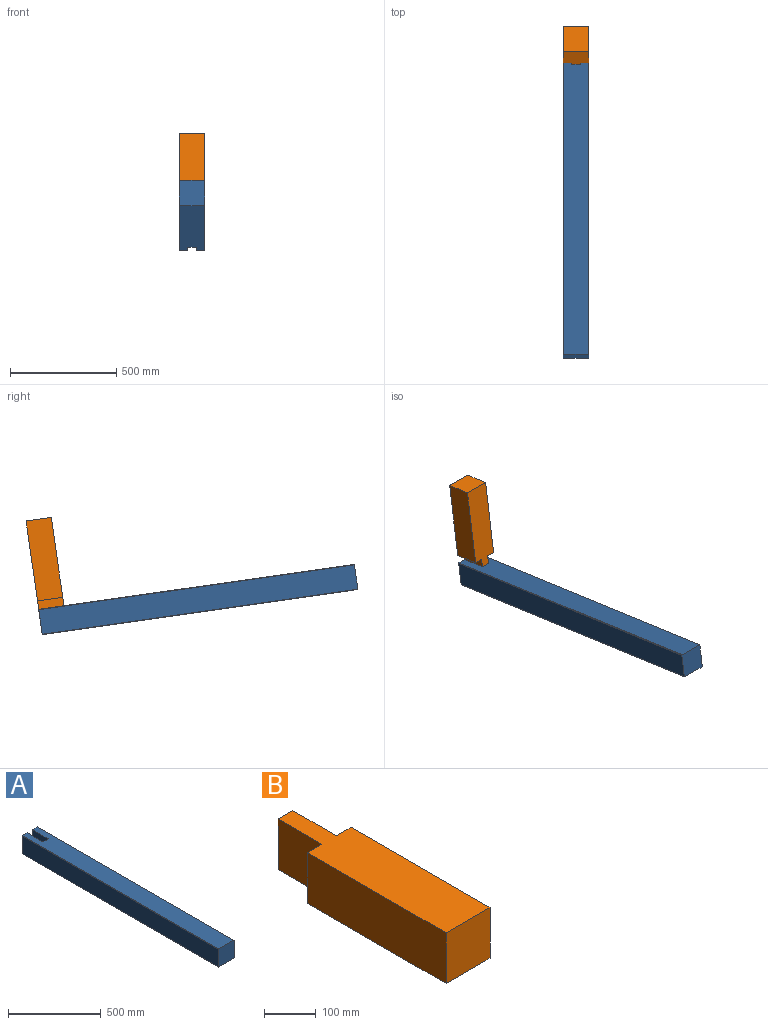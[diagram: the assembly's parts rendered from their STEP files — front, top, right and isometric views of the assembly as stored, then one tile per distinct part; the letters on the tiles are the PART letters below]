
ASSEMBLY  parts=2 mates=2
PART A: 14 faces, bbox 120x1500x120 mm
  f0: plane 120x40mm, normal (0,1,0), area 4796mm2, adj f1,f2,f4,f7,f10,f13
  f1: plane 1500x116mm, normal (0,0,-1), area 169200mm2, adj f0,f5,f6,f7,f8,f11,f12,f13
  f2: plane 1500x116mm, normal (0,0,1), area 169200mm2, adj f0,f5,f6,f9,f10,f11,f12,f13
  f3: plane 1500x116mm, normal (-1,0,0), area 174000mm2, adj f5,f6,f8,f9
  f4: plane 1500x116mm, normal (1,0,0), area 174000mm2, adj f0,f5,f7,f10
  f5: plane 120x120mm, normal (0,-1,0), area 14392mm2, adj f1,f2,f3,f4,f7,f8,f9,f10
  f6: plane 120x40mm, normal (0,1,0), area 4796mm2, adj f1,f2,f3,f8,f9,f11
  f7: plane 1500x2mm, normal (0.71,0,-0.71), area 4242.6mm2, adj f0,f1,f4,f5
  f8: plane 1500x2mm, normal (-0.71,0,-0.71), area 4242.6mm2, adj f1,f3,f5,f6
  f9: plane 1500x2mm, normal (-0.71,0,0.71), area 4242.6mm2, adj f2,f3,f5,f6
  f10: plane 1500x2mm, normal (0.71,0,0.71), area 4242.6mm2, adj f0,f2,f4,f5
  f11: plane 120x120mm, normal (1,0,0), area 14400mm2, adj f1,f2,f6,f12
  f12: plane 120x40mm, normal (0,1,0), area 4800mm2, adj f1,f2,f11,f13
  f13: plane 120x120mm, normal (-1,0,0), area 14400mm2, adj f0,f1,f2,f12
PART B: 10 faces, bbox 120x500x120 mm
  f0: plane 380x120mm, normal (-1,0,0), area 45600mm2, adj f1,f4,f5,f9
  f1: plane 500x120mm, normal (0,0,-1), area 50400mm2, adj f0,f2,f3,f5,f6,f7,f8,f9
  f2: plane 380x120mm, normal (1,0,0), area 45600mm2, adj f1,f4,f5,f7
  f3: plane 120x40mm, normal (0,1,0), area 4800mm2, adj f1,f4,f6,f8
  f4: plane 500x120mm, normal (0,0,1), area 50400mm2, adj f0,f2,f3,f5,f6,f7,f8,f9
  f5: plane 120x120mm, normal (0,-1,0), area 14400mm2, adj f0,f1,f2,f4
  f6: plane 120x120mm, normal (1,0,0), area 14400mm2, adj f1,f3,f4,f7
  f7: plane 120x40mm, normal (0,1,0), area 4800mm2, adj f1,f2,f4,f6
  f8: plane 120x120mm, normal (-1,0,0), area 14400mm2, adj f1,f3,f4,f9
  f9: plane 120x40mm, normal (0,1,0), area 4800mm2, adj f0,f1,f4,f8
PLACE A rot(axis=(-1,0,0),8.1deg) t=(-113.08,-53.55,156.76)mm
PLACE B rot(axis=(-1,0,0),98.1deg) t=(-113.08,-166.6,213.89)mm
MATE planar A.f12 <-> B.f1  axis (0,0.99,-0.14) through (-33.08,-155.36,292.53)mm
MATE planar B.f6 <-> A.f13  axis (1,0,0) through (-33.08,-149.63,332.68)mm
